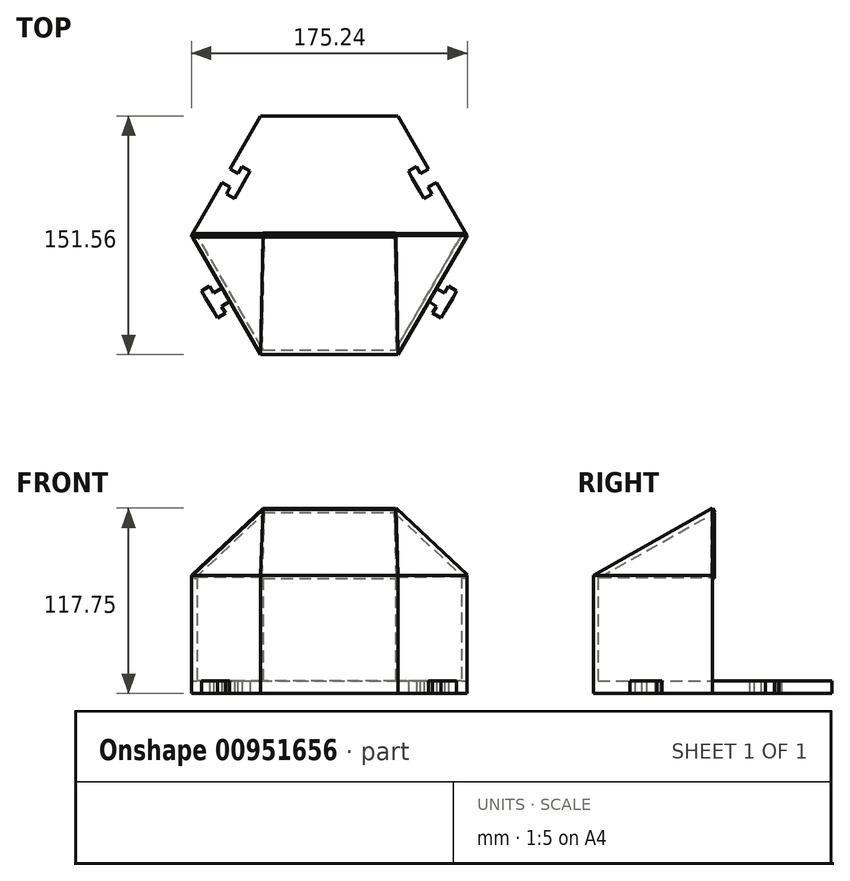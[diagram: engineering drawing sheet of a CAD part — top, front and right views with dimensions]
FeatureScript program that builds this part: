
annotation { "Feature Type Name" : "Feature", "Feature Type Description" : "" }
export const myFeature = defineFeature(function(context is Context, id is Id, definition is map)
    precondition{}
    {
        {
            var Q0;
            Q0=qCreatedBy(makeId("Top.planeOp"),FACE);
            var sketch = newSketch(context, id + "F0", { "sketchPlane" : qUnion([Q0])});
            skCircle(sketch, "E0.cCircle", {"center": v(0, 0) * mm, "radius": 75.78 * mm, "construction": true});
            skLineSegment(sketch, "E0.0", {"start": v(-43.75, 75.78) * mm, "end": v(43.75, 75.78) * mm});
            skLineSegment(sketch, "E0.1", {"start": v(43.75, 75.78) * mm, "end": v(87.5, 0) * mm});
            skLineSegment(sketch, "E0.2", {"start": v(87.5, 0) * mm, "end": v(43.75, -75.78) * mm});
            skLineSegment(sketch, "E0.3", {"start": v(43.75, -75.78) * mm, "end": v(-43.75, -75.78) * mm});
            skLineSegment(sketch, "E0.4", {"start": v(-43.75, -75.78) * mm, "end": v(-87.5, 0) * mm});
            skLineSegment(sketch, "E0.5", {"start": v(-87.5, 0) * mm, "end": v(-43.75, 75.78) * mm});
            skPoint(sketch, "E0.0.midPoint", {"position": v(0, 75.78) * mm});
            skLineSegment(sketch, "E1.0", {"start": v(-84.04, 0) * mm, "end": v(-42.02, 72.78) * mm});
            skLineSegment(sketch, "E1.1", {"start": v(42.02, 72.78) * mm, "end": v(84.04, 0) * mm});
            skLineSegment(sketch, "E1.2", {"start": v(84.04, 0) * mm, "end": v(42.02, -72.78) * mm});
            skLineSegment(sketch, "E1.3", {"start": v(-42.02, 72.78) * mm, "end": v(42.02, 72.78) * mm});
            skLineSegment(sketch, "E1.4", {"start": v(42.02, -72.78) * mm, "end": v(-42.02, -72.78) * mm});
            skLineSegment(sketch, "E1.5", {"start": v(-42.02, -72.78) * mm, "end": v(-84.04, 0) * mm});
            skLineSegment(sketch, "E2", {"start": v(-87.5, 0) * mm, "end": v(-84.04, 0) * mm});
            skLineSegment(sketch, "E3", {"start": v(84.04, 0) * mm, "end": v(87.5, 0) * mm});
            skLineSegment(sketch, "E4", {"start": v(0, 0) * mm, "end": v(0, 72.78) * mm, "construction": true});
            skLineSegment(sketch, "E5", {"start": v(0, 0) * mm, "end": v(42.02, 72.78) * mm, "construction": true});
            skLineSegment(sketch, "E6", {"start": v(0, 0) * mm, "end": v(-42.02, 72.78) * mm, "construction": true});
            skLineSegment(sketch, "E7", {"start": v(0, 36.39) * mm, "end": v(0, 72.78) * mm, "construction": true});
            skLineSegment(sketch, "E8.bottom", {"start": v(25, 48.33) * mm, "end": v(-25, 48.33) * mm});
            skLineSegment(sketch, "E8.top", {"start": v(25, 60.83) * mm, "end": v(-25, 60.83) * mm});
            skLineSegment(sketch, "E8.left", {"start": v(25, 48.33) * mm, "end": v(25, 60.83) * mm});
            skLineSegment(sketch, "E8.right", {"start": v(-25, 48.33) * mm, "end": v(-25, 60.83) * mm});
            skPoint(sketch, "E8.middle", {"position": v(0, 54.58) * mm});
            skLineSegment(sketch, "E9", {"start": v(-65.63, 37.89) * mm, "end": v(-55.16, 32) * mm, "construction": true});
            skLineSegment(sketch, "E10", {"start": v(-55.16, 32) * mm, "end": v(-52.71, 36.37) * mm, "construction": true});
            skLineSegment(sketch, "E11", {"start": v(-55.16, 32) * mm, "end": v(-57.62, 27.65) * mm, "construction": true});
            skLineSegment(sketch, "E12", {"start": v(-52.71, 36.37) * mm, "end": v(-63.12, 42.22) * mm});
            skLineSegment(sketch, "E13", {"start": v(-57.62, 27.65) * mm, "end": v(-52.71, 36.37) * mm});
            skLineSegment(sketch, "E14", {"start": v(-65.63, 37.89) * mm, "end": v(-68.13, 33.56) * mm});
            skLineSegment(sketch, "E15", {"start": v(-57.62, 27.65) * mm, "end": v(-68.13, 33.56) * mm});
            skLineSegment(sketch, "E16.MirrorCS", {"start": v(55.16, 32) * mm, "end": v(57.62, 27.65) * mm});
            skLineSegment(sketch, "E17.MirrorCS", {"start": v(55.16, 32) * mm, "end": v(52.71, 36.37) * mm});
            skLineSegment(sketch, "E18.MirrorCS", {"start": v(57.62, 27.65) * mm, "end": v(68.13, 33.56) * mm});
            skLineSegment(sketch, "E19.MirrorCS", {"start": v(87.5, 0) * mm, "end": v(43.75, 75.78) * mm});
            skLineSegment(sketch, "E20.MirrorCS", {"start": v(52.71, 36.37) * mm, "end": v(63.12, 42.22) * mm});
            skLineSegment(sketch, "E21", {"start": v(-62.87, 30.6) * mm, "end": v(-65.32, 26.25) * mm});
            skLineSegment(sketch, "E22", {"start": v(-57.62, 27.65) * mm, "end": v(-60.07, 23.3) * mm});
            skLineSegment(sketch, "E23", {"start": v(-65.32, 26.25) * mm, "end": v(-60.07, 23.3) * mm});
            skLineSegment(sketch, "E24.MirrorCS", {"start": v(-52.71, 36.37) * mm, "end": v(-50.26, 40.72) * mm});
            skLineSegment(sketch, "E25.MirrorCS", {"start": v(-57.97, 39.32) * mm, "end": v(-55.52, 43.68) * mm});
            skLineSegment(sketch, "E26.MirrorCS", {"start": v(-55.52, 43.68) * mm, "end": v(-50.26, 40.72) * mm});
            skLineSegment(sketch, "E27.MirrorCS", {"start": v(57.97, 39.32) * mm, "end": v(55.52, 43.68) * mm});
            skLineSegment(sketch, "E28.MirrorCS", {"start": v(55.52, 43.68) * mm, "end": v(50.26, 40.72) * mm});
            skLineSegment(sketch, "E29.MirrorCS", {"start": v(52.71, 36.37) * mm, "end": v(50.26, 40.72) * mm});
            skLineSegment(sketch, "E30.MirrorCS", {"start": v(57.62, 27.65) * mm, "end": v(60.07, 23.3) * mm});
            skLineSegment(sketch, "E31.MirrorCS", {"start": v(62.87, 30.6) * mm, "end": v(65.32, 26.25) * mm});
            skLineSegment(sketch, "E32.MirrorCS", {"start": v(65.32, 26.25) * mm, "end": v(60.07, 23.3) * mm});
            skLineSegment(sketch, "E33.MirrorCS", {"start": v(-78.45, -39.68) * mm, "end": v(-68.12, -33.56) * mm});
            skLineSegment(sketch, "E34.MirrorCS", {"start": v(-73.33, -36.65) * mm, "end": v(-75.88, -32.34) * mm});
            skLineSegment(sketch, "E35.MirrorCS", {"start": v(-75.88, -32.34) * mm, "end": v(-80.95, -35.46) * mm});
            skLineSegment(sketch, "E36.MirrorCS", {"start": v(-78.45, -39.68) * mm, "end": v(-81, -35.38) * mm});
            skLineSegment(sketch, "E37.MirrorCS", {"start": v(-78.45, -39.68) * mm, "end": v(-73.4, -48.2) * mm});
            skLineSegment(sketch, "E38.MirrorCS", {"start": v(-73.4, -48.2) * mm, "end": v(-70.88, -52.4) * mm});
            skLineSegment(sketch, "E39.MirrorCS", {"start": v(-65.74, -49.4) * mm, "end": v(-70.88, -52.4) * mm});
            skLineSegment(sketch, "E40.MirrorCS", {"start": v(-68.26, -45.15) * mm, "end": v(-65.74, -49.4) * mm});
            skLineSegment(sketch, "E41.MirrorCS", {"start": v(-73.4, -48.2) * mm, "end": v(-63.12, -42.1) * mm});
            skLineSegment(sketch, "E42", {"start": v(-73.4, -48.2) * mm, "end": v(-68.26, -45.15) * mm});
            skPoint(sketch, "E42.endSnap0", {"position": v(-68.26, -45.15) * mm});
            skLineSegment(sketch, "E43.MirrorCS", {"start": v(68.26, -45.15) * mm, "end": v(65.74, -49.4) * mm});
            skLineSegment(sketch, "E44.MirrorCS", {"start": v(65.74, -49.4) * mm, "end": v(70.88, -52.4) * mm});
            skLineSegment(sketch, "E45.MirrorCS", {"start": v(73.4, -48.2) * mm, "end": v(70.88, -52.4) * mm});
            skLineSegment(sketch, "E46.MirrorCS", {"start": v(73.4, -48.2) * mm, "end": v(63.12, -42.1) * mm});
            skLineSegment(sketch, "E47.MirrorCS", {"start": v(78.45, -39.68) * mm, "end": v(73.4, -48.2) * mm});
            skLineSegment(sketch, "E48.MirrorCS", {"start": v(78.45, -39.68) * mm, "end": v(68.12, -33.56) * mm});
            skLineSegment(sketch, "E49.MirrorCS", {"start": v(73.33, -36.65) * mm, "end": v(75.88, -32.34) * mm});
            skLineSegment(sketch, "E50.MirrorCS", {"start": v(75.88, -32.34) * mm, "end": v(80.95, -35.46) * mm});
            skLineSegment(sketch, "E51.MirrorCS", {"start": v(78.45, -39.68) * mm, "end": v(81, -35.38) * mm});
            skLineSegment(sketch, "E52", {"start": v(-68.13, 33.56) * mm, "end": v(-65.63, 32.15) * mm});
            skLineSegment(sketch, "E53", {"start": v(68.13, 33.56) * mm, "end": v(65.5, 32.09) * mm});
            skSolve(sketch);
        }
        {
            var Q0;
            Q0=makeQuery(id+"F0.imprint","IMPRINT",FACE,{"disambiguationData":[TD([[makeQuery(id+"F0.imprint","IMPRINT",EDGE,{"derivedFrom":sQuery(id+"F0.wireOp",EDGE,"E1.0")}),-1.0]])]});
            extrude(context, id + "F1", {"entities" : qUnion([Q0]), "depth" : 8 * mm, "offsetDistance" : 25 * mm});
        }
        {
            var Q0;
            Q0=makeQuery(id+"F0.imprint","IMPRINT",FACE,{"disambiguationData":[TD([[makeQuery(id+"F0.imprint","IMPRINT",EDGE,{"derivedFrom":sQuery(id+"F0.wireOp",EDGE,"E0.2")}),-1.0]])]});
            extrude(context, id + "F2", {"entities" : qUnion([Q0]), "operationType" : NewBodyOperationType.ADD, "depth" : 75 * mm, "offsetDistance" : 25 * mm});
        }
        {
            var Q0;
            Q0=qCreatedBy(makeId("Front.planeOp"),FACE);
            var sketch = newSketch(context, id + "F3", { "sketchPlane" : qUnion([Q0])});
            skLineSegment(sketch, "E54", {"start": v(0, 0) * mm, "end": v(0, 144.27) * mm, "construction": true});
            skLineSegment(sketch, "E55", {"start": v(0, 144.27) * mm, "end": v(-94, 144.27) * mm, "construction": true});
            skLineSegment(sketch, "E56", {"start": v(0, 144.27) * mm, "end": v(81.74, 144.27) * mm});
            skLineSegment(sketch, "E57", {"start": v(0, 0) * mm, "end": v(0, 75) * mm, "construction": true});
            skLineSegment(sketch, "E58", {"start": v(0, 75) * mm, "end": v(0, 114.5) * mm, "construction": true});
            skLineSegment(sketch, "E59", {"start": v(0, 75) * mm, "end": v(-87.5, 75) * mm, "construction": true});
            skLineSegment(sketch, "E60", {"start": v(0, 114.5) * mm, "end": v(42.02, 114.5) * mm, "construction": true});
            skLineSegment(sketch, "E61", {"start": v(0, 114.5) * mm, "end": v(-42.02, 114.5) * mm});
            skLineSegment(sketch, "E62", {"start": v(0, 75) * mm, "end": v(-84.04, 75) * mm, "construction": true});
            skLineSegment(sketch, "E63", {"start": v(-42.02, 114.5) * mm, "end": v(-84.04, 75) * mm});
            skLineSegment(sketch, "E64", {"start": v(-42.02, 114.5) * mm, "end": v(-42.02, 117.5) * mm, "construction": true});
            skLineSegment(sketch, "E65", {"start": v(-42.02, 117.5) * mm, "end": v(-87.5, 75) * mm});
            skLineSegment(sketch, "E66", {"start": v(-42.02, 117.5) * mm, "end": v(0, 117.5) * mm});
            skLineSegment(sketch, "E67.MirrorCS", {"start": v(42.02, 117.5) * mm, "end": v(87.5, 75) * mm});
            skLineSegment(sketch, "E68.MirrorCS", {"start": v(42.02, 114.5) * mm, "end": v(84.04, 75) * mm});
            skLineSegment(sketch, "E69.MirrorCS", {"start": v(42.02, 117.5) * mm, "end": v(0, 117.5) * mm});
            skLineSegment(sketch, "E70.MirrorCS", {"start": v(0, 114.5) * mm, "end": v(42.02, 114.5) * mm});
            skLineSegment(sketch, "E71", {"start": v(87.5, 75) * mm, "end": v(84.04, 75) * mm});
            skLineSegment(sketch, "E72", {"start": v(-84.04, 75) * mm, "end": v(-87.5, 75) * mm});
            skSolve(sketch);
        }
        {
            var Q0;
            Q0=makeQuery(id+"F0.imprint","IMPRINT",FACE,{"disambiguationData":[TD([[makeQuery(id+"F0.imprint","IMPRINT",EDGE,{"derivedFrom":sQuery(id+"F0.wireOp",EDGE,"E0.0")}),-1.0]])]});
            extrude(context, id + "F4", {"entities" : qUnion([Q0]), "operationType" : NewBodyOperationType.ADD, "oppositeDirection" : true, "depth" : -8 * mm, "offsetDistance" : 25 * mm});
        }
        {
            var Q0;
            Q0=makeQuery(id+"F2.opExtrude","CAP_EDGE",EDGE,{"disambiguationData":[OSD([sQuery(id+"F0.wireOp",EDGE,"E0.3")])],"isStart":false});
            var Q1;
            Q1=sQuery(id+"F3.wireOp",VERTEX,"E66.end");
            cPlane(context, id + "F5", {"entities" : qUnion([Q0, Q1]), "cplaneType" : CPlaneType.LINE_ANGLE, "offset" : 25 * mm, "angle" : 0 * degree, "width" : 150 * mm, "height" : 150 * mm});
        }
        {
            var Q0;
            Q0=qCreatedBy(id+"F5.planeOp",FACE);
            var sketch = newSketch(context, id + "F6", { "sketchPlane" : qUnion([Q0])});
            skLineSegment(sketch, "E73", {"start": v(0, 29.4) * mm, "end": v(43.75, 29.4) * mm});
            skLineSegment(sketch, "E74", {"start": v(0, 29.4) * mm, "end": v(-43.75, 29.4) * mm});
            skLineSegment(sketch, "E75", {"start": v(-43.75, 29.4) * mm, "end": v(-42.02, -57.48) * mm});
            skLineSegment(sketch, "E76", {"start": v(43.75, 29.4) * mm, "end": v(42.02, -57.48) * mm});
            skLineSegment(sketch, "E77", {"start": v(-42.02, -57.48) * mm, "end": v(42.02, -57.48) * mm});
            skSolve(sketch);
        }
        {
            var Q0;
            Q0=makeQuery(id+"F6.imprint","IMPRINT",FACE,{"disambiguationData":[TD([[makeQuery(id+"F6.imprint","IMPRINT",EDGE,{"derivedFrom":sQuery(id+"F6.wireOp",EDGE,"E73")}),-1.0]])]});
            extrude(context, id + "F7", {"entities" : qUnion([Q0]), "operationType" : NewBodyOperationType.ADD, "depth" : 3 * mm, "offsetDistance" : 25 * mm});
        }
        {
            var Q0;
            Q0=makeQuery(id+"F3.imprint","IMPRINT",FACE,{"disambiguationData":[TD([[makeQuery(id+"F3.imprint","IMPRINT",EDGE,{"derivedFrom":sQuery(id+"F3.wireOp",EDGE,"E61")}),-1.0]])]});
            extrude(context, id + "F8", {"entities" : qUnion([Q0]), "operationType" : NewBodyOperationType.ADD, "depth" : 1 * mm, "offsetDistance" : 25 * mm});
        }
        {
            var Q0;
            Q0=makeQuery(id+"F8.opExtrude","CAP_EDGE",EDGE,{"disambiguationData":[OSD([sQuery(id+"F3.wireOp",EDGE,"E65")])],"isStart":true});
            var Q1;
            Q1=makeQuery(id+"F7.boolean.opBoolean","MERGE",VERTEX,{"derivedFrom":[makeQuery(id+"F2.opExtrude","CAP_VERTEX",VERTEX,{"disambiguationData":[OSD([sQuery(id+"F0.wireOp",EDGE,"E0.3"),sQuery(id+"F0.wireOp",EDGE,"E0.4")])],"isStart":false}),makeQuery(id+"F7.opExtrude","CAP_VERTEX",VERTEX,{"disambiguationData":[OSD([sQuery(id+"F6.wireOp",EDGE,"E74"),sQuery(id+"F6.wireOp",EDGE,"E75")])],"isStart":true})]});
            cPlane(context, id + "F9", {"entities" : qUnion([Q0, Q1]), "cplaneType" : CPlaneType.LINE_ANGLE, "offset" : 25 * mm, "angle" : 0 * degree, "width" : 150 * mm, "height" : 150 * mm});
        }
        {
            var Q0;
            Q0=qCreatedBy(id+"F9.planeOp",FACE);
            var sketch = newSketch(context, id + "F10", { "sketchPlane" : qUnion([Q0])});
            skLineSegment(sketch, "E78", {"start": v(-25.66, 35.61) * mm, "end": v(30.99, -31.08) * mm});
            skLineSegment(sketch, "E79", {"start": v(-25.66, 35.61) * mm, "end": v(33.23, 55.79) * mm});
            skLineSegment(sketch, "E80", {"start": v(33.23, 55.79) * mm, "end": v(30.99, -31.08) * mm});
            skSolve(sketch);
        }
        {
            var Q0;
            Q0=qSketchRegion(id+"F10",true);
            extrude(context, id + "F11", {"entities" : qUnion([Q0]), "operationType" : NewBodyOperationType.ADD, "depth" : -3 * mm, "offsetDistance" : 25 * mm});
        }
        {
            var Q0;
            Q0=makeQuery(id+"F8.opExtrude","CAP_EDGE",EDGE,{"disambiguationData":[OSD([sQuery(id+"F3.wireOp",EDGE,"E67.MirrorCS")])],"isStart":false});
            var Q1;
            Q1=makeQuery(id+"F7.boolean.opBoolean","MERGE",VERTEX,{"derivedFrom":[makeQuery(id+"F2.opExtrude","CAP_VERTEX",VERTEX,{"disambiguationData":[OSD([sQuery(id+"F0.wireOp",EDGE,"E0.2"),sQuery(id+"F0.wireOp",EDGE,"E0.3")])],"isStart":false}),makeQuery(id+"F7.opExtrude","CAP_VERTEX",VERTEX,{"disambiguationData":[OSD([sQuery(id+"F6.wireOp",EDGE,"E73"),sQuery(id+"F6.wireOp",EDGE,"E76")])],"isStart":true})]});
            cPlane(context, id + "F12", {"entities" : qUnion([Q0, Q1]), "cplaneType" : CPlaneType.LINE_ANGLE, "offset" : 25 * mm, "angle" : 0 * degree, "width" : 150 * mm, "height" : 150 * mm});
        }
        {
            var Q0;
            Q0=qCreatedBy(id+"F12.planeOp",FACE);
            var sketch = newSketch(context, id + "F13", { "sketchPlane" : qUnion([Q0])});
            skLineSegment(sketch, "E81", {"start": v(-32.88, -56.36) * mm, "end": v(25.94, -35.98) * mm});
            skLineSegment(sketch, "E82", {"start": v(25.94, -35.98) * mm, "end": v(-30.94, 30.51) * mm});
            skLineSegment(sketch, "E83", {"start": v(-30.94, 30.51) * mm, "end": v(-32.88, -56.36) * mm});
            skSolve(sketch);
        }
        {
            var Q0;
            Q0=qSketchRegion(id+"F13",true);
            extrude(context, id + "F14", {"entities" : qUnion([Q0]), "operationType" : NewBodyOperationType.ADD, "depth" : 3 * mm, "offsetDistance" : 25 * mm});
        }
        {
            var Q0;
            Q0=makeQuery(id+"F0.imprint","IMPRINT",FACE,{"disambiguationData":[TD([[makeQuery(id+"F0.imprint","IMPRINT",EDGE,{"derivedFrom":sQuery(id+"F0.wireOp",EDGE,"E8.bottom")}),-1.0]])]});
            extrude(context, id + "F15", {"entities" : qUnion([Q0]), "operationType" : NewBodyOperationType.ADD, "depth" : 8 * mm, "offsetDistance" : 25 * mm});
        }
        {
            var Q0;
            {var subQ5=sQuery(id+"F0.wireOp",EDGE,"E35.MirrorCS");Q0=makeQuery(id+"F0.imprint","IMPRINT",FACE,{"disambiguationData":[TD([[makeQuery(id+"F0.imprint","IMPRINT",EDGE,{"derivedFrom":subQ5}),1.0]])]});}
            var Q1;
            {var subQ4=sQuery(id+"F0.wireOp",EDGE,"E37.MirrorCS");Q1=makeQuery(id+"F0.imprint","IMPRINT",FACE,{"disambiguationData":[TD([[makeQuery(id+"F0.imprint","IMPRINT",EDGE,{"derivedFrom":subQ4}),1.0]])]});}
            var Q2;
            {var subQ0=sQuery(id+"F0.wireOp",EDGE,"E38.MirrorCS");Q2=makeQuery(id+"F0.imprint","IMPRINT",FACE,{"disambiguationData":[TD([[makeQuery(id+"F0.imprint","IMPRINT",EDGE,{"derivedFrom":subQ0}),1.0]])]});}
            var Q3;
            {var subQ5=sQuery(id+"F0.wireOp",EDGE,"E50.MirrorCS");Q3=makeQuery(id+"F0.imprint","IMPRINT",FACE,{"disambiguationData":[TD([[makeQuery(id+"F0.imprint","IMPRINT",EDGE,{"derivedFrom":subQ5}),-1.0]])]});}
            var Q4;
            {var subQ0=sQuery(id+"F0.wireOp",EDGE,"E47.MirrorCS");Q4=makeQuery(id+"F0.imprint","IMPRINT",FACE,{"disambiguationData":[TD([[makeQuery(id+"F0.imprint","IMPRINT",EDGE,{"derivedFrom":subQ0}),-1.0]])]});}
            var Q5;
            {var subQ0=sQuery(id+"F0.wireOp",EDGE,"E43.MirrorCS");Q5=makeQuery(id+"F0.imprint","IMPRINT",FACE,{"disambiguationData":[TD([[makeQuery(id+"F0.imprint","IMPRINT",EDGE,{"derivedFrom":subQ0}),1.0]])]});}
            extrude(context, id + "F16", {"entities" : qUnion([Q0, Q1, Q2, Q3, Q4, Q5]), "operationType" : NewBodyOperationType.ADD, "depth" : 8 * mm, "offsetDistance" : 25 * mm});
        }
        {
            var Q0;
            {var subQ4=sQuery(id+"F0.wireOp",EDGE,"E2");Q0=makeQuery(id+"F0.imprint","IMPRINT",FACE,{"disambiguationData":[TD([[makeQuery(id+"F0.imprint","IMPRINT",EDGE,{"derivedFrom":subQ4}),1.0]])]});}
            var Q1;
            {var subQ0=sQuery(id+"F0.wireOp",EDGE,"E3");Q1=makeQuery(id+"F0.imprint","IMPRINT",FACE,{"disambiguationData":[TD([[makeQuery(id+"F0.imprint","IMPRINT",EDGE,{"derivedFrom":subQ0}),1.0]])]});}
            extrude(context, id + "F17", {"entities" : qUnion([Q0, Q1]), "operationType" : NewBodyOperationType.ADD, "depth" : 8 * mm, "offsetDistance" : 25 * mm});
        }
    });
